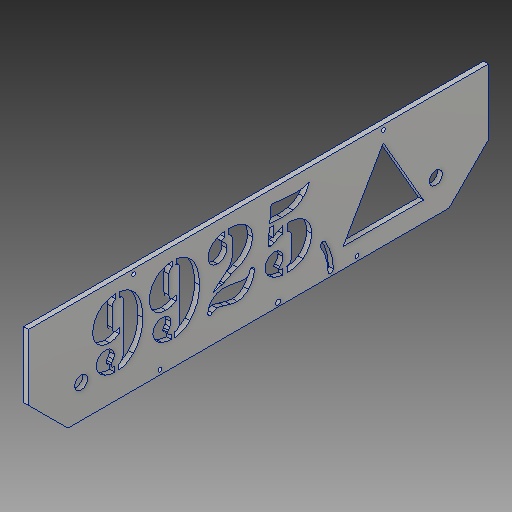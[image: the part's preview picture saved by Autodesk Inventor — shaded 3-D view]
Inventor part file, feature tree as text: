
AUTODESK INVENTOR PART (.ipt)
format: ipt  version: 2019 (Build 230136000, 136)  size: 550,912 bytes
history: native  units: in
note: dims shown in document units (in); Inventor stores cm internally (conversion verified against a paired STEP export)
features: sketch x6, extrude x4, chamfer x2, hole x2, projected_geometry x1
ambient origin geometry x8: Origin, YZ Plane, XZ Plane, XY Plane, X Axis, Y Axis, Z Axis, Center Point
bodies: Solid1 (feature_tree)
feature tree (15):
  extrude  "Extrusion1"  Depth=17.5in
  chamfer  "Chamfer1"  Distance=0.1875in
  chamfer  "Chamfer2"  Distance=1.5in Angle=45.0deg
  hole  "Hole3"  [1 undecoded]
  sketch  "Sketch9"  dims[d3=1.25in]
  hole  "Hole4"  [1 undecoded]
  extrude  "Extrusion6"  Depth=0.603in
  extrude  "Extrusion7"  Depth=0.125in
  extrude  "Extrusion8"  Depth=0.63in
  sketch  "Sketch12"  dims[d11=1.5in d12=0.125in d13=45.0deg d22=6.517in d23=0.125in d24=0.603in d25=0.125in d26=0.63in d27=6.517in d28=0.125in d29=0.603in d30=6.517in d31=0.125in d32=0.63in d33=6.517in d110=0.175in d111=0.175in d112=4.0in d113=4.0in d114=0.175in d115=0.175in d116=0.15in d117=0.75in d118=0.375in d119=0.25in d120=0.5635in d121=1.0in d122=0.8108in d123=5.0in d124=5.0in d125=8.0in d126=0.15in d127=0.2in d128=0.75in d129=0.375in d130=0.25in d131=0.5635in d132=1.0in d133=0.8108in d134=2.0in d135=0.2in d137=1.0in d138=0.0in d139=0.2in d140=1.0in d141=1.0in d142=0.0in d143=0.75in d144=0.75in d145=0.6033in d146=4.0in d147=0.0in d148=0.0in d149=0.4in d152=0.05in d153=0.05in d154=0.2426in d155=4.7244in d157=360.0deg d160=4.7244in d161=0.4in d162=0.05in d163=0.05in d164=0.2426in d165=360.0deg d167=4.7244in d168=0.4in d169=0.05in d170=0.05in d171=0.2426in d172=360.0deg]
  sketch  "Sketch1"  dims[d0=4.0in d1=17.5in]
  sketch  "Sketch8"  dims[d2=0.501in]
  projected_geometry  "Projected Loop7"
  sketch  "Sketch10"  dims[d4=2.0in]
  sketch  "Sketch11"  dims[d5=2.0in d6=0.1875in d7=0.0in d8=1.5in d9=0.125in d10=45.0deg]
note: 2 required parameter values undecoded (feature->parameter linkage not recoverable at this tier; creation-order binding heuristic only, values carry confidence <= 0.55)
